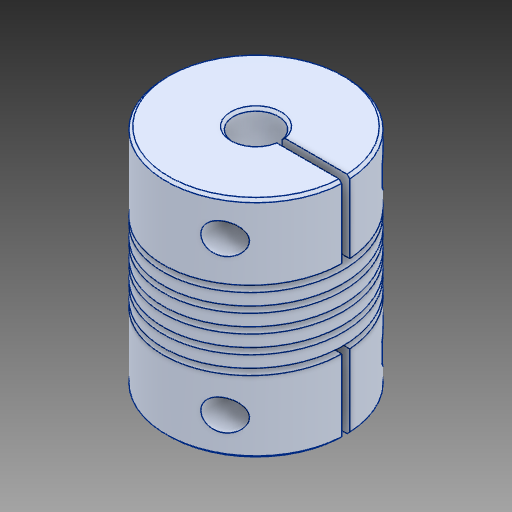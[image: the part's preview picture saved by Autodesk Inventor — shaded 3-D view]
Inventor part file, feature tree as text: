
AUTODESK INVENTOR PART (.ipt)
format: ipt  version: 2017 (Build 210142000, 142)  size: 397,824 bytes
history: mixed  units: mm
features: chamfer x1, imported_body x1
ambient origin geometry x8: Origin, YZ Plane, XZ Plane, XY Plane, X Axis, Y Axis, Z Axis, Center Point
bodies: Solid1 (imported_parasolid)
feature tree (2):
  chamfer  "Chamfer1"  [1 undecoded]
  imported_body  NMx_Import_Brep_tag  [imported B-rep: ~5 faces, bbox_mm=None]
note: 1 required parameter value undecoded (feature->parameter linkage not recoverable at this tier; creation-order binding heuristic only, values carry confidence <= 0.55)
